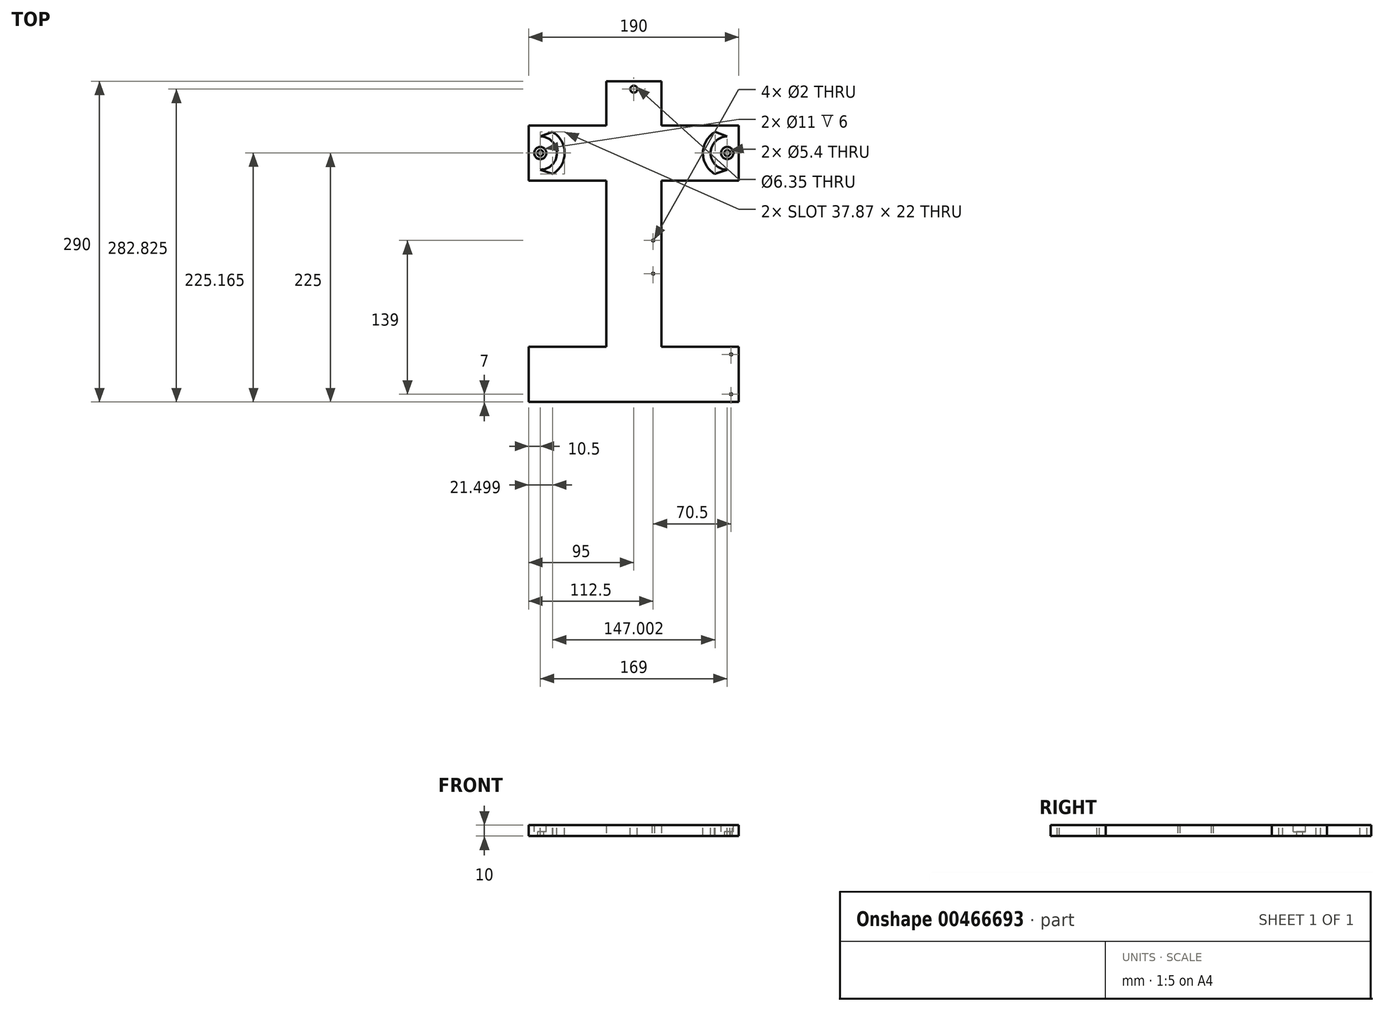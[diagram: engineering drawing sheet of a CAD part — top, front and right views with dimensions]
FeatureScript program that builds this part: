
annotation { "Feature Type Name" : "Feature", "Feature Type Description" : "" }
export const myFeature = defineFeature(function(context is Context, id is Id, definition is map)
    precondition{}
    {
        {
            var Q0;
            Q0=qCreatedBy(makeId("Top.planeOp"),FACE);
            var sketch = newSketch(context, id + "F0", { "sketchPlane" : qUnion([Q0])});
            skLineSegment(sketch, "E0.bottom", {"start": v(25, 75) * mm, "end": v(-25, 75) * mm});
            skLineSegment(sketch, "E0.top", {"start": v(25, -75) * mm, "end": v(-25, -75) * mm});
            skLineSegment(sketch, "E0.left", {"start": v(25, 75) * mm, "end": v(25, -75) * mm});
            skLineSegment(sketch, "E0.right", {"start": v(-25, 75) * mm, "end": v(-25, -75) * mm});
            skPoint(sketch, "E0.middle", {"position": v(0, 0) * mm});
            skLineSegment(sketch, "E1.top", {"start": v(25, 125) * mm, "end": v(-25, 125) * mm});
            skLineSegment(sketch, "E1.left", {"start": v(25, 75) * mm, "end": v(25, 125) * mm});
            skLineSegment(sketch, "E1.right", {"start": v(-25, 75) * mm, "end": v(-25, 125) * mm});
            skLineSegment(sketch, "E2.bottom", {"start": v(25, 75) * mm, "end": v(95, 75) * mm});
            skLineSegment(sketch, "E2.top", {"start": v(25, 125) * mm, "end": v(95, 125) * mm});
            skLineSegment(sketch, "E2.right", {"start": v(95, 75) * mm, "end": v(95, 125) * mm});
            skLineSegment(sketch, "E3.bottom", {"start": v(-25, 75) * mm, "end": v(-95, 75) * mm});
            skLineSegment(sketch, "E3.top", {"start": v(-25, 125) * mm, "end": v(-95, 125) * mm});
            skLineSegment(sketch, "E3.right", {"start": v(-95, 75) * mm, "end": v(-95, 125) * mm});
            skLineSegment(sketch, "E4.bottom", {"start": v(-25, -75) * mm, "end": v(-95, -75) * mm});
            skLineSegment(sketch, "E4.top", {"start": v(-25, -125) * mm, "end": v(-95, -125) * mm});
            skLineSegment(sketch, "E4.left", {"start": v(-25, -75) * mm, "end": v(-25, -125) * mm});
            skLineSegment(sketch, "E4.right", {"start": v(-95, -75) * mm, "end": v(-95, -125) * mm});
            skLineSegment(sketch, "E5.bottom", {"start": v(25, -75) * mm, "end": v(95, -75) * mm});
            skLineSegment(sketch, "E5.top", {"start": v(25, -125) * mm, "end": v(95, -125) * mm});
            skLineSegment(sketch, "E5.left", {"start": v(25, -75) * mm, "end": v(25, -125) * mm});
            skLineSegment(sketch, "E5.right", {"start": v(95, -75) * mm, "end": v(95, -125) * mm});
            skLineSegment(sketch, "E6.bottom", {"start": v(-25, -75) * mm, "end": v(25, -75) * mm});
            skLineSegment(sketch, "E6.top", {"start": v(-25, -125) * mm, "end": v(25, -125) * mm});
            skLineSegment(sketch, "E7.bottom", {"start": v(-25, 125) * mm, "end": v(25, 125) * mm});
            skLineSegment(sketch, "E7.top", {"start": v(-25, 165) * mm, "end": v(25, 165) * mm});
            skLineSegment(sketch, "E7.left", {"start": v(-25, 125) * mm, "end": v(-25, 165) * mm});
            skLineSegment(sketch, "E7.right", {"start": v(25, 125) * mm, "end": v(25, 165) * mm});
            skSolve(sketch);
        }
        {
            var Q0;
            Q0=qSketchRegion(id+"F0",true);
            extrude(context, id + "F1", {"entities" : qUnion([Q0]), "depth" : 10 * mm});
        }
        {
            var Q0;
            Q0=makeQuery(id+"F1.opExtrude","CAP_FACE",FACE,{"disambiguationData":[OSD([sQuery(id+"F0.wireOp",EDGE,"E0.left"),sQuery(id+"F0.wireOp",EDGE,"E0.right"),sQuery(id+"F0.wireOp",EDGE,"E2.bottom"),sQuery(id+"F0.wireOp",EDGE,"E2.top"),sQuery(id+"F0.wireOp",EDGE,"E2.right"),sQuery(id+"F0.wireOp",EDGE,"E3.bottom"),sQuery(id+"F0.wireOp",EDGE,"E3.top"),sQuery(id+"F0.wireOp",EDGE,"E3.right"),sQuery(id+"F0.wireOp",EDGE,"E4.bottom"),sQuery(id+"F0.wireOp",EDGE,"E4.top"),sQuery(id+"F0.wireOp",EDGE,"E4.right"),sQuery(id+"F0.wireOp",EDGE,"E5.bottom"),sQuery(id+"F0.wireOp",EDGE,"E5.top"),sQuery(id+"F0.wireOp",EDGE,"E5.right"),sQuery(id+"F0.wireOp",EDGE,"E6.top"),sQuery(id+"F0.wireOp",EDGE,"E7.top"),sQuery(id+"F0.wireOp",EDGE,"E7.left"),sQuery(id+"F0.wireOp",EDGE,"E7.right")])],"isStart":false});
            var sketch = newSketch(context, id + "F2", { "sketchPlane" : qUnion([Q0])});
            skCircle(sketch, "E8", {"center": v(0, 157.82) * mm, "radius": 3.18 * mm});
            skPoint(sketch, "E8.centerSnap0", {"position": v(25, 145) * mm});
            skSolve(sketch);
        }
        {
            var Q0;
            Q0=qSketchRegion(id+"F2",true);
            extrude(context, id + "F3", {"entities" : qUnion([Q0]), "operationType" : NewBodyOperationType.REMOVE, "endBound" : BoundingType.THROUGH_ALL, "oppositeDirection" : true, "depth" : 25 * mm});
        }
        {
            var Q0;
            Q0=makeQuery(id+"F1.opExtrude","CAP_FACE",FACE,{"disambiguationData":[OSD([sQuery(id+"F0.wireOp",EDGE,"E0.left"),sQuery(id+"F0.wireOp",EDGE,"E0.right"),sQuery(id+"F0.wireOp",EDGE,"E2.bottom"),sQuery(id+"F0.wireOp",EDGE,"E2.top"),sQuery(id+"F0.wireOp",EDGE,"E2.right"),sQuery(id+"F0.wireOp",EDGE,"E3.bottom"),sQuery(id+"F0.wireOp",EDGE,"E3.top"),sQuery(id+"F0.wireOp",EDGE,"E3.right"),sQuery(id+"F0.wireOp",EDGE,"E4.bottom"),sQuery(id+"F0.wireOp",EDGE,"E4.top"),sQuery(id+"F0.wireOp",EDGE,"E4.right"),sQuery(id+"F0.wireOp",EDGE,"E5.bottom"),sQuery(id+"F0.wireOp",EDGE,"E5.top"),sQuery(id+"F0.wireOp",EDGE,"E5.right"),sQuery(id+"F0.wireOp",EDGE,"E6.top"),sQuery(id+"F0.wireOp",EDGE,"E7.top"),sQuery(id+"F0.wireOp",EDGE,"E7.left"),sQuery(id+"F0.wireOp",EDGE,"E7.right")])],"isStart":false});
            var sketch = newSketch(context, id + "F4", { "sketchPlane" : qUnion([Q0])});
            skCircle(sketch, "E9", {"center": v(-84.5, 100) * mm, "radius": 5.5 * mm});
            skPoint(sketch, "E9.centerSnap0", {"position": v(-95, 100) * mm});
            skSolve(sketch);
        }
        {
            var Q0;
            Q0=qSketchRegion(id+"F4",true);
            extrude(context, id + "F5", {"entities" : qUnion([Q0]), "operationType" : NewBodyOperationType.REMOVE, "endBound" : BoundingType.THROUGH_ALL, "oppositeDirection" : true, "depth" : 25 * mm});
        }
        {
            var Q0;
            Q0=makeQuery(id+"F1.opExtrude","CAP_FACE",FACE,{"disambiguationData":[OSD([sQuery(id+"F0.wireOp",EDGE,"E0.left"),sQuery(id+"F0.wireOp",EDGE,"E0.right"),sQuery(id+"F0.wireOp",EDGE,"E2.bottom"),sQuery(id+"F0.wireOp",EDGE,"E2.top"),sQuery(id+"F0.wireOp",EDGE,"E2.right"),sQuery(id+"F0.wireOp",EDGE,"E3.bottom"),sQuery(id+"F0.wireOp",EDGE,"E3.top"),sQuery(id+"F0.wireOp",EDGE,"E3.right"),sQuery(id+"F0.wireOp",EDGE,"E4.bottom"),sQuery(id+"F0.wireOp",EDGE,"E4.top"),sQuery(id+"F0.wireOp",EDGE,"E4.right"),sQuery(id+"F0.wireOp",EDGE,"E5.bottom"),sQuery(id+"F0.wireOp",EDGE,"E5.top"),sQuery(id+"F0.wireOp",EDGE,"E5.right"),sQuery(id+"F0.wireOp",EDGE,"E6.top"),sQuery(id+"F0.wireOp",EDGE,"E7.top"),sQuery(id+"F0.wireOp",EDGE,"E7.left"),sQuery(id+"F0.wireOp",EDGE,"E7.right")])],"isStart":false});
            var sketch = newSketch(context, id + "F6", { "sketchPlane" : qUnion([Q0])});
            skCircle(sketch, "E10", {"center": v(84.5, 100) * mm, "radius": 5.5 * mm});
            skPoint(sketch, "E10.centerSnap0", {"position": v(95, 100) * mm});
            skSolve(sketch);
        }
        {
            var Q0;
            Q0=qSketchRegion(id+"F6",true);
            extrude(context, id + "F7", {"entities" : qUnion([Q0]), "operationType" : NewBodyOperationType.REMOVE, "endBound" : BoundingType.THROUGH_ALL, "oppositeDirection" : true, "depth" : 25 * mm});
        }
        {
            var Q0;
            Q0=makeQuery(id+"F1.opExtrude","CAP_FACE",FACE,{"disambiguationData":[OSD([sQuery(id+"F0.wireOp",EDGE,"E0.left"),sQuery(id+"F0.wireOp",EDGE,"E0.right"),sQuery(id+"F0.wireOp",EDGE,"E2.bottom"),sQuery(id+"F0.wireOp",EDGE,"E2.top"),sQuery(id+"F0.wireOp",EDGE,"E2.right"),sQuery(id+"F0.wireOp",EDGE,"E3.bottom"),sQuery(id+"F0.wireOp",EDGE,"E3.top"),sQuery(id+"F0.wireOp",EDGE,"E3.right"),sQuery(id+"F0.wireOp",EDGE,"E4.bottom"),sQuery(id+"F0.wireOp",EDGE,"E4.top"),sQuery(id+"F0.wireOp",EDGE,"E4.right"),sQuery(id+"F0.wireOp",EDGE,"E5.bottom"),sQuery(id+"F0.wireOp",EDGE,"E5.top"),sQuery(id+"F0.wireOp",EDGE,"E5.right"),sQuery(id+"F0.wireOp",EDGE,"E6.top"),sQuery(id+"F0.wireOp",EDGE,"E7.top"),sQuery(id+"F0.wireOp",EDGE,"E7.left"),sQuery(id+"F0.wireOp",EDGE,"E7.right")])],"isStart":false});
            var sketch = newSketch(context, id + "F8", { "sketchPlane" : qUnion([Q0])});
            skArc(sketch, "E11", {"start": v(84.5, 85) * mm, "mid": v(69.5, 100) * mm, "end": v(84.5, 115) * mm});
            skArc(sketch, "E12.0", {"start": v(73.02, 81.23) * mm, "mid": v(62.5, 100.32) * mm, "end": v(73.58, 119.1) * mm});
            skLineSegment(sketch, "E13", {"start": v(84.5, 85) * mm, "end": v(73.02, 81.23) * mm});
            skLineSegment(sketch, "E14", {"start": v(84.5, 115) * mm, "end": v(73.58, 119.1) * mm});
            skArc(sketch, "E15.MirrorCS", {"start": v(-73.02, 81.23) * mm, "mid": v(-62.5, 100.32) * mm, "end": v(-73.58, 119.1) * mm});
            skArc(sketch, "E16.MirrorCS", {"start": v(-84.5, 85) * mm, "mid": v(-69.5, 100) * mm, "end": v(-84.5, 115) * mm});
            skLineSegment(sketch, "E17.MirrorCS", {"start": v(-84.5, 85) * mm, "end": v(-73.02, 81.23) * mm});
            skLineSegment(sketch, "E18.MirrorCS", {"start": v(-84.5, 115) * mm, "end": v(-73.58, 119.1) * mm});
            skSolve(sketch);
        }
        {
            var Q0;
            Q0=qSketchRegion(id+"F8",true);
            extrude(context, id + "F9", {"entities" : qUnion([Q0]), "operationType" : NewBodyOperationType.REMOVE, "endBound" : BoundingType.THROUGH_ALL, "oppositeDirection" : true, "depth" : 25 * mm});
        }
        {
            var Q0;
            Q0=makeQuery(id+"F8.imprint","IMPRINT",FACE,{"disambiguationData":[TD([[makeQuery(id+"F8.imprint","IMPRINT",EDGE,{"derivedFrom":sQuery(id+"F8.wireOp",EDGE,"E11")}),-1.0]])]});
            var sketch = newSketch(context, id + "F10", { "sketchPlane" : qUnion([Q0])});
            skPoint(sketch, "E19", {"position": v(88, -118) * mm});
            skPoint(sketch, "E20", {"position": v(88, -82) * mm});
            skSolve(sketch);
        }
        {
            var Q0;
            Q0=sQuery(id+"FYF6CrEqlv0wlKG_1.1.F10.wireOp",VERTEX,"E20");
            var Q1;
            Q1=sQuery(id+"FYF6CrEqlv0wlKG_1.1.F10.wireOp",VERTEX,"E19");
            var Q2;
            Q2=sQuery(id+"F10.wireOp",VERTEX,"E20");
            var Q3;
            Q3=sQuery(id+"F10.wireOp",VERTEX,"E19");
            var Q4;
            Q4=makeQuery(id+"F1.opExtrude","SWEPT_BODY",BODY,{"disambiguationData":[OSD([sQuery(id+"F0.wireOp",EDGE,"E0.left"),sQuery(id+"F0.wireOp",EDGE,"E0.right"),sQuery(id+"F0.wireOp",EDGE,"E2.bottom"),sQuery(id+"F0.wireOp",EDGE,"E2.top"),sQuery(id+"F0.wireOp",EDGE,"E2.right"),sQuery(id+"F0.wireOp",EDGE,"E3.bottom"),sQuery(id+"F0.wireOp",EDGE,"E3.top"),sQuery(id+"F0.wireOp",EDGE,"E3.right"),sQuery(id+"F0.wireOp",EDGE,"E4.bottom"),sQuery(id+"F0.wireOp",EDGE,"E4.top"),sQuery(id+"F0.wireOp",EDGE,"E4.right"),sQuery(id+"F0.wireOp",EDGE,"E5.bottom"),sQuery(id+"F0.wireOp",EDGE,"E5.top"),sQuery(id+"F0.wireOp",EDGE,"E5.right"),sQuery(id+"F0.wireOp",EDGE,"E6.top"),sQuery(id+"F0.wireOp",EDGE,"E7.top"),sQuery(id+"F0.wireOp",EDGE,"E7.left"),sQuery(id+"F0.wireOp",EDGE,"E7.right")])]});
            hole(context, id + "F11", {"style" : HoleStyle.SIMPLE, "endStyle" : HoleEndStyle.THROUGH, "holeDiameter" : 2 * mm, "isTappedThrough" : true, "tappedDepth" : 12 * mm, "tapClearance" : 3, "locations" : qUnion([Q0, Q1, Q2, Q3]), "scope" : qUnion([Q4])});
        }
        {
            var Q0;
            Q0=makeQuery(id+"F0.imprint","IMPRINT",FACE,{"disambiguationData":[TD([[makeQuery(id+"F0.imprint","IMPRINT",EDGE,{"derivedFrom":sQuery(id+"F0.wireOp",EDGE,"E0.left")}),-1.0]])]});
            var sketch = newSketch(context, id + "F12", { "sketchPlane" : qUnion([Q0])});
            skPoint(sketch, "E21", {"position": v(17.5, -9) * mm});
            skPoint(sketch, "E22", {"position": v(17.5, 21) * mm});
            skSolve(sketch);
        }
        {
            var Q0;
            Q0=sQuery(id+"F12.wireOp",VERTEX,"E22");
            var Q1;
            Q1=sQuery(id+"F12.wireOp",VERTEX,"E21");
            var Q2;
            Q2=makeQuery(id+"F1.opExtrude","SWEPT_BODY",BODY,{"disambiguationData":[OSD([sQuery(id+"F0.wireOp",EDGE,"E0.left"),sQuery(id+"F0.wireOp",EDGE,"E0.right"),sQuery(id+"F0.wireOp",EDGE,"E2.bottom"),sQuery(id+"F0.wireOp",EDGE,"E2.top"),sQuery(id+"F0.wireOp",EDGE,"E2.right"),sQuery(id+"F0.wireOp",EDGE,"E3.bottom"),sQuery(id+"F0.wireOp",EDGE,"E3.top"),sQuery(id+"F0.wireOp",EDGE,"E3.right"),sQuery(id+"F0.wireOp",EDGE,"E4.bottom"),sQuery(id+"F0.wireOp",EDGE,"E4.top"),sQuery(id+"F0.wireOp",EDGE,"E4.right"),sQuery(id+"F0.wireOp",EDGE,"E5.bottom"),sQuery(id+"F0.wireOp",EDGE,"E5.top"),sQuery(id+"F0.wireOp",EDGE,"E5.right"),sQuery(id+"F0.wireOp",EDGE,"E6.top"),sQuery(id+"F0.wireOp",EDGE,"E7.top"),sQuery(id+"F0.wireOp",EDGE,"E7.left"),sQuery(id+"F0.wireOp",EDGE,"E7.right")])]});
            hole(context, id + "F13", {"style" : HoleStyle.SIMPLE, "endStyle" : HoleEndStyle.THROUGH, "oppositeDirection" : true, "holeDiameter" : 2 * mm, "isTappedThrough" : true, "tappedDepth" : 12 * mm, "tapClearance" : 3, "locations" : qUnion([Q0, Q1]), "scope" : qUnion([Q2])});
        }
        {
            var Q0;
            Q0=qCreatedBy(makeId("Top.planeOp"),FACE);
            var sketch = newSketch(context, id + "F14", { "sketchPlane" : qUnion([Q0])});
            skCircle(sketch, "E23", {"center": v(84.5, 100) * mm, "radius": 5.5 * mm});
            skCircle(sketch, "E24.0", {"center": v(84.5, 100) * mm, "radius": 2.7 * mm});
            skCircle(sketch, "E25", {"center": v(-84.5, 100) * mm, "radius": 5.5 * mm});
            skCircle(sketch, "E26.0", {"center": v(-84.5, 100) * mm, "radius": 2.7 * mm});
            skSolve(sketch);
        }
        {
            var Q0;
            Q0 = qSketchRegion(id + "F14", true);
            extrude(context, id + "F15", {"entities" : qUnion([Q0]), "operationType" : NewBodyOperationType.ADD, "depth" : 4 * mm});
        }
        {
            var Q0;
            Q0 = qSketchRegion(id + "F14", true);
            extrude(context, id + "F16", {"entities" : qUnion([Q0]), "operationType" : NewBodyOperationType.ADD, "depth" : 4 * mm});
        }
    });
